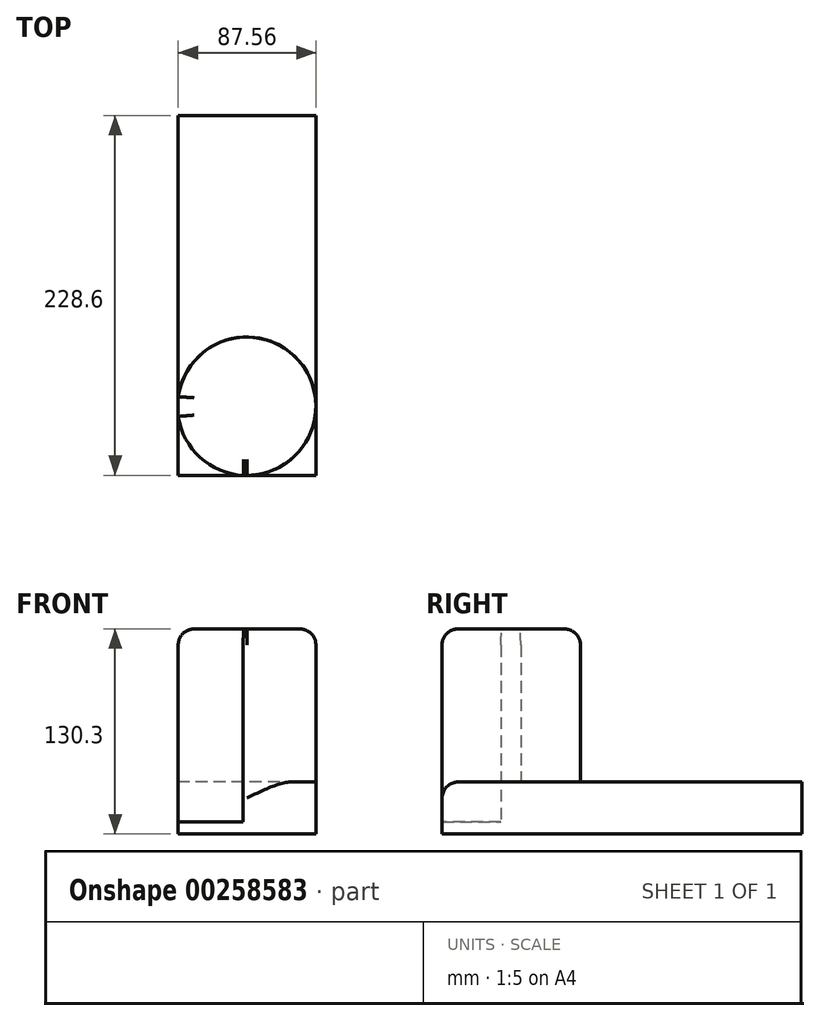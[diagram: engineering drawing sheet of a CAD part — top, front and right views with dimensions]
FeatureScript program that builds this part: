
annotation { "Feature Type Name" : "Feature", "Feature Type Description" : "" }
export const myFeature = defineFeature(function(context is Context, id is Id, definition is map)
    precondition{}
    {
        {
            var Q0;
            Q0=qCreatedBy(makeId("Front.planeOp"),FACE);
            var sketch = newSketch(context, id + "F0", { "sketchPlane" : qUnion([Q0])});
            skLineSegment(sketch, "E0.bottom", {"start": v(43.78, -16.5) * mm, "end": v(-43.78, -16.5) * mm});
            skLineSegment(sketch, "E0.top", {"start": v(43.78, 16.5) * mm, "end": v(-43.78, 16.5) * mm});
            skLineSegment(sketch, "E0.left", {"start": v(43.78, -16.5) * mm, "end": v(43.78, 16.5) * mm});
            skLineSegment(sketch, "E0.right", {"start": v(-43.78, -16.5) * mm, "end": v(-43.78, 16.5) * mm});
            skPoint(sketch, "E0.middle", {"position": v(0, 0) * mm});
            skSolve(sketch);
        }
        {
            var Q0;
            Q0=makeQuery(id+"F0.imprint","IMPRINT",FACE,{"disambiguationData":[TD([[makeQuery(id+"F0.imprint","IMPRINT",EDGE,{"derivedFrom":sQuery(id+"F0.wireOp",EDGE,"E0.bottom")}),-1.0]])]});
            extrude(context, id + "F1", {"entities" : qUnion([Q0]), "depth" : 228.6 * mm});
        }
        {
            var Q0;
            Q0=makeQuery(id+"F1.opExtrude","SWEPT_FACE",FACE,{"disambiguationData":[OSD([sQuery(id+"F0.wireOp",EDGE,"E0.top")])]});
            var sketch = newSketch(context, id + "F2", { "sketchPlane" : qUnion([Q0])});
            skArc(sketch, "E1", {"start": v(0, -228.6) * mm, "mid": v(32.78, -155.73) * mm, "end": v(-43.78, -178.6) * mm});
            skSolve(sketch);
        }
        {
            var Q0;
            {var subQ0=sQuery(id+"F2.wireOp",EDGE,"E1");Q0=makeQuery(id+"F2.imprint","IMPRINT",FACE,{"disambiguationData":[TD([[makeQuery(id+"F2.imprint","IMPRINT",EDGE,{"derivedFrom":subQ0}),1.0]])]});}
            extrude(context, id + "F3", {"entities" : qUnion([Q0]), "operationType" : NewBodyOperationType.REMOVE, "oppositeDirection" : true, "depth" : 25.4 * mm});
        }
        {
            var Q0;
            Q0=makeQuery(id+"F3.boolean.opBoolean","COPY",FACE,{"derivedFrom":makeQuery(id+"F3.opExtrude","CAP_FACE",FACE,{"disambiguationData":[OSD([sQuery(id+"F0.wireOp",EDGE,"E0.top"),sQuery(id+"F0.wireOp",EDGE,"E0.right"),sQuery(id+"F2.wireOp",EDGE,"E1")])],"isStart":false})});
            var sketch = newSketch(context, id + "F4", { "sketchPlane" : qUnion([Q0])});
            skCircle(sketch, "E2", {"center": v(-0.27, -184.67) * mm, "radius": 43.98 * mm});
            skSolve(sketch);
        }
        {
            var Q0;
            {var subQ6=makeQuery(id+"F3.boolean.opBoolean","COPY",EDGE,{"derivedFrom":makeQuery(id+"F3.opExtrude","CAP_EDGE",EDGE,{"disambiguationData":[OSD([sQuery(id+"F2.wireOp",EDGE,"E1")])],"isStart":false})});Q0=makeQuery(id+"F4.imprint","IMPRINT",FACE,{"disambiguationData":[TD([[makeQuery(id+"F4.imprint","IMPRINT",EDGE,{"derivedFrom":subQ6}),1.0]])]});}
            extrude(context, id + "F5", {"entities" : qUnion([Q0]), "operationType" : NewBodyOperationType.ADD, "depth" : 122.68 * mm});
        }
        {
            var Q0;
            Q0=makeQuery(id+"F5.opExtrude","CAP_EDGE",EDGE,{"disambiguationData":[OSD([sQuery(id+"F4.wireOp",EDGE,"E2")])],"isStart":false});
            var Q1;
            Q1=makeQuery(id+"F5.opExtrude","CAP_FACE",FACE,{"disambiguationData":[OSD([sQuery(id+"F0.wireOp",EDGE,"E0.top"),sQuery(id+"F0.wireOp",EDGE,"E0.right"),sQuery(id+"F2.wireOp",EDGE,"E1"),sQuery(id+"F4.wireOp",EDGE,"E2")])],"isStart":false});
            fillet(context, id + "F6", {"entities" : qUnion([Q0, Q1]), "radius" : 10.16 * mm, "tangentPropagation" : true, "allowEdgeOverflow" : false});
        }
        {
            var Q0;
            Q0=makeQuery(id+"F1.opExtrude","CAP_EDGE",EDGE,{"disambiguationData":[OSD([sQuery(id+"F0.wireOp",EDGE,"E0.top")])],"isStart":false});
            fillet(context, id + "F7", {"entities" : qUnion([Q0]), "radius" : 10.16 * mm, "tangentPropagation" : true, "allowEdgeOverflow" : false});
        }
    });
